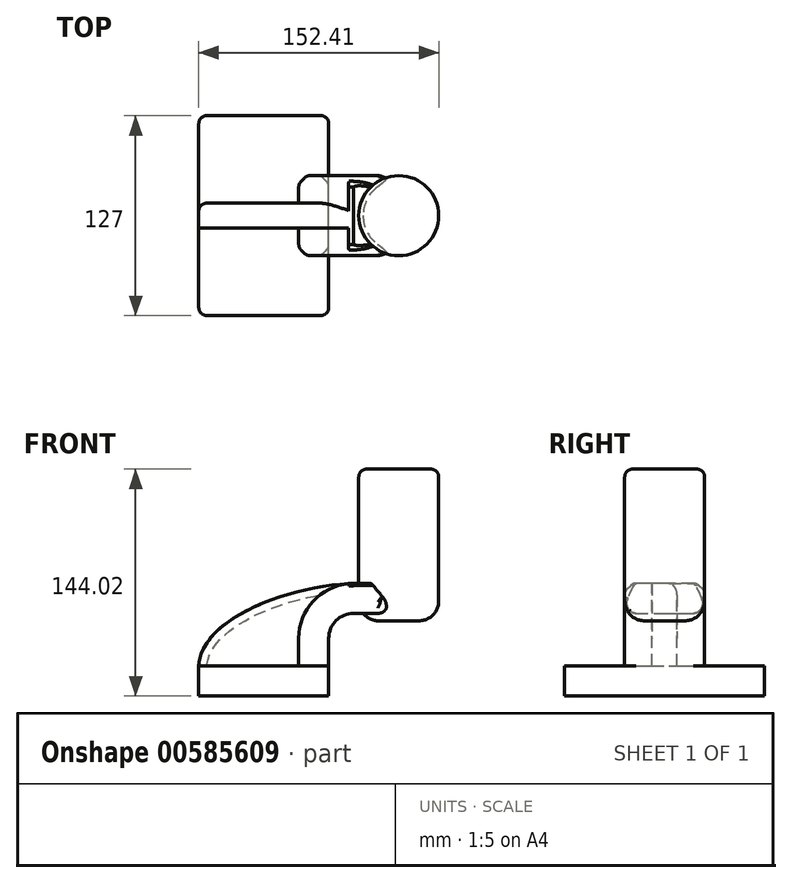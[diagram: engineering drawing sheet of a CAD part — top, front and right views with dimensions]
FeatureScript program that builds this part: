
annotation { "Feature Type Name" : "Feature", "Feature Type Description" : "" }
export const myFeature = defineFeature(function(context is Context, id is Id, definition is map)
    precondition{}
    {
        {
            var Q0;
            Q0=qCreatedBy(makeId("Front.planeOp"),FACE);
            var sketch = newSketch(context, id + "F0", { "sketchPlane" : qUnion([Q0])});
            skLineSegment(sketch, "E0.rect.bottom", {"start": v(-41.28, 9.52) * mm, "end": v(41.28, 9.52) * mm});
            skLineSegment(sketch, "E0.rect.top", {"start": v(-41.28, -9.52) * mm, "end": v(41.28, -9.52) * mm});
            skLineSegment(sketch, "E0.rect.left", {"start": v(-41.28, 9.52) * mm, "end": v(-41.28, -9.52) * mm});
            skLineSegment(sketch, "E0.rect.right", {"start": v(41.28, 9.52) * mm, "end": v(41.28, -9.52) * mm});
            skPoint(sketch, "E0.rect.middle", {"position": v(0, 0) * mm});
            skLineSegment(sketch, "E1", {"start": v(41.28, 9.52) * mm, "end": v(41.28, 27) * mm});
            skArc(sketch, "E2", {"start": v(41.28, 27) * mm, "mid": v(45.92, 38.23) * mm, "end": v(57.15, 42.88) * mm});
            skLineSegment(sketch, "E3", {"start": v(57.15, 42.88) * mm, "end": v(85.72, 42.88) * mm});
            skLineSegment(sketch, "E4.rect.bottom", {"start": v(60.32, 38.1) * mm, "end": v(111.12, 38.1) * mm});
            skLineSegment(sketch, "E4.rect.top", {"start": v(60.32, 66.68) * mm, "end": v(111.12, 66.68) * mm});
            skLineSegment(sketch, "E4.rect.left", {"start": v(60.32, 38.1) * mm, "end": v(60.32, 66.68) * mm});
            skLineSegment(sketch, "E4.rect.right", {"start": v(111.13, 38.1) * mm, "end": v(111.12, 66.68) * mm});
            skPoint(sketch, "E4.rect.middle", {"position": v(85.72, 52.39) * mm});
            skLineSegment(sketch, "E5.0", {"start": v(57.15, 61.93) * mm, "end": v(85.72, 61.93) * mm});
            skArc(sketch, "E5.1", {"start": v(22.23, 27) * mm, "mid": v(32.45, 51.7) * mm, "end": v(57.15, 61.93) * mm});
            skLineSegment(sketch, "E5.2", {"start": v(22.23, 9.52) * mm, "end": v(22.23, 27) * mm});
            skLineSegment(sketch, "E6", {"start": v(85.72, 38.1) * mm, "end": v(85.72, 66.68) * mm});
            skFitSpline(sketch, "E7", {"points": [v(-41.28, 9.53) * mm, v(57.15, 61.93) * mm], "startDerivative": vector(5.2, 92.34) * mm, "endDerivative": vector(120.92, 4.22) * mm});
            skSolve(sketch);
        }
        {
            var Q0;
            Q0=makeQuery(id+"F0.imprint","IMPRINT",FACE,{"disambiguationData":[TD([[makeQuery(id+"F0.imprint","IMPRINT",EDGE,{"derivedFrom":sQuery(id+"F0.wireOp",EDGE,"E0.rect.top")}),1.0]])]});
            extrude(context, id + "F1", {"entities" : qUnion([Q0]), "endBound" : BoundingType.SYMMETRIC, "depth" : 127 * mm});
        }
        {
            var Q0;
            {var subQ9=sQuery(id+"F0.wireOp",EDGE,"E1");Q0=makeQuery(id+"F0.imprint","IMPRINT",FACE,{"disambiguationData":[TD([[makeQuery(id+"F0.imprint","IMPRINT",EDGE,{"derivedFrom":subQ9}),1.0]])]});}
            var Q1;
            {var subQ0=sQuery(id+"F0.wireOp",EDGE,"E6");var subQ1=sQuery(id+"F0.wireOp",EDGE,"E3");var subQ2=makeQuery(id+"F0.imprint","INTERSECT",VERTEX,{"derivedFrom":[subQ1,subQ0]});Q1=makeQuery(id+"F0.imprint","IMPRINT",FACE,{"disambiguationData":[TD([[makeQuery(id+"F0.imprint","IMPRINT",EDGE,{"disambiguationData":[TD([[subQ2,1.0]])],"derivedFrom":subQ1}),1.0]])]});}
            extrude(context, id + "F2", {"entities" : qUnion([Q0, Q1]), "operationType" : NewBodyOperationType.ADD, "endBound" : BoundingType.SYMMETRIC, "depth" : 50.8 * mm});
        }
        {
            var Q0;
            {var subQ3=sQuery(id+"F0.wireOp",EDGE,"E5.2");Q0=makeQuery(id+"F0.imprint","IMPRINT",FACE,{"disambiguationData":[TD([[makeQuery(id+"F0.imprint","IMPRINT",EDGE,{"derivedFrom":subQ3}),1.0]])]});}
            extrude(context, id + "F3", {"entities" : qUnion([Q0]), "operationType" : NewBodyOperationType.ADD, "endBound" : BoundingType.SYMMETRIC, "depth" : 15.88 * mm});
        }
        {
            var Q0;
            {var subQ5=sQuery(id+"F0.wireOp",EDGE,"E4.rect.right");Q0=makeQuery(id+"F0.imprint","IMPRINT",FACE,{"disambiguationData":[TD([[makeQuery(id+"F0.imprint","IMPRINT",EDGE,{"derivedFrom":subQ5}),1.0]])]});}
            var Q1;
            Q1=sQuery(id+"F0.wireOp",EDGE,"E6");
            revolve(context, id + "F4", {"operationType" : NewBodyOperationType.ADD, "entities" : qUnion([Q0]), "axis" : qUnion([Q1]), "revolveType" : RevolveType.FULL});
        }
        {
            var Q0;
            Q0=makeQuery(id+"F1.opExtrude","CAP_EDGE",EDGE,{"disambiguationData":[OSD([sQuery(id+"F0.wireOp",EDGE,"E0.rect.right")])],"isStart":false});
            var Q1;
            Q1=makeQuery(id+"F1.opExtrude","CAP_EDGE",EDGE,{"disambiguationData":[OSD([sQuery(id+"F0.wireOp",EDGE,"E0.rect.left")])],"isStart":false});
            var Q2;
            Q2=makeQuery(id+"F1.opExtrude","CAP_EDGE",EDGE,{"disambiguationData":[OSD([sQuery(id+"F0.wireOp",EDGE,"E0.rect.right")])],"isStart":true});
            var Q3;
            Q3=makeQuery(id+"F1.opExtrude","CAP_EDGE",EDGE,{"disambiguationData":[OSD([sQuery(id+"F0.wireOp",EDGE,"E0.rect.left")])],"isStart":true});
            fillet(context, id + "F5", {"entities" : qUnion([Q0, Q1, Q2, Q3]), "radius" : 5.08 * mm, "tangentPropagation" : true, "allowEdgeOverflow" : false});
        }
        {
            var Q0;
            Q0=makeQuery(id+"F4.opRevolve","SWEPT_FACE",FACE,{"disambiguationData":[OSD([sQuery(id+"F0.wireOp",EDGE,"E4.rect.top")])]});
            extrude(context, id + "F6", {"entities" : qUnion([Q0]), "operationType" : NewBodyOperationType.ADD, "depth" : 67.82 * mm, "offsetDistance" : 25.4 * mm});
        }
        {
            var Q0;
            Q0=makeQuery(id+"F6.opExtrude","CAP_EDGE",EDGE,{"disambiguationData":[OSD([sQuery(id+"F0.wireOp",EDGE,"E4.rect.top"),sQuery(id+"F0.wireOp",EDGE,"E4.rect.right")])],"isStart":false});
            fillet(context, id + "F7", {"entities" : qUnion([Q0]), "radius" : 5.08 * mm, "tangentPropagation" : true, "allowEdgeOverflow" : false});
        }
        {
            var Q0;
            Q0=makeQuery(id+"F2.opExtrude","CAP_EDGE",EDGE,{"disambiguationData":[OSD([sQuery(id+"F0.wireOp",EDGE,"E5.1")])],"isStart":true});
            chamfer(context, id + "F8", {"entities" : qUnion([Q0]), "width" : 5.08 * mm, "tangentPropagation" : true});
        }
        {
            var Q0;
            Q0=makeQuery(id+"F2.opExtrude","CAP_EDGE",EDGE,{"disambiguationData":[OSD([sQuery(id+"F0.wireOp",EDGE,"E5.1")])],"isStart":false});
            chamfer(context, id + "F9", {"entities" : qUnion([Q0]), "width" : 5.08 * mm, "tangentPropagation" : true});
        }
        {
            var Q0;
            Q0=makeQuery(id+"F2.opExtrude","CAP_EDGE",EDGE,{"disambiguationData":[OSD([sQuery(id+"F0.wireOp",EDGE,"E2")])],"isStart":false});
            chamfer(context, id + "F10", {"entities" : qUnion([Q0]), "width" : 5.08 * mm, "tangentPropagation" : true});
        }
        {
            var Q0;
            Q0=makeQuery(id+"F2.opExtrude","CAP_EDGE",EDGE,{"disambiguationData":[OSD([sQuery(id+"F0.wireOp",EDGE,"E2")])],"isStart":true});
            chamfer(context, id + "F11", {"entities" : qUnion([Q0]), "width" : 5.08 * mm, "tangentPropagation" : true});
        }
        {
            var Q0;
            {var subQ0=sQuery(id+"F0.wireOp",EDGE,"E7");var subQ1=sQuery(id+"F0.wireOp",EDGE,"E5.2");var subQ2=sQuery(id+"F0.wireOp",EDGE,"E5.1");var subQ3=sQuery(id+"F0.wireOp",EDGE,"E0.rect.bottom");Q0=makeQuery(id+"F9.opChamfer","BLEND_EDGE",EDGE,{"blendedFrom":[makeQuery(id+"F2.opExtrude","CAP_EDGE",EDGE,{"disambiguationData":[OSD([subQ2])],"isStart":false}),makeQuery(id+"F3.boolean.opBoolean","SPLIT",FACE,{"disambiguationData":[TD([makeQuery(id+"F3.opExtrude","CAP_FACE",FACE,{"disambiguationData":[OSD([subQ3,subQ2,subQ1,subQ0])],"isStart":false})])],"derivedFrom":makeQuery(id+"F2.opExtrude","SWEPT_FACE",FACE,{"disambiguationData":[OSD([subQ2])]})})],"blendedInto":[makeQuery(id+"F3.boolean.opBoolean","SPLIT",FACE,{"disambiguationData":[TD([makeQuery(id+"F3.opExtrude","CAP_FACE",FACE,{"disambiguationData":[OSD([subQ3,subQ2,subQ1,subQ0])],"isStart":false})])],"derivedFrom":makeQuery(id+"F2.opExtrude","SWEPT_FACE",FACE,{"disambiguationData":[OSD([subQ2])]})})]});}
            fillet(context, id + "F12", {"entities" : qUnion([Q0]), "radius" : 5.08 * mm, "tangentPropagation" : true, "allowEdgeOverflow" : false});
        }
        {
            var Q0;
            {var subQ0=sQuery(id+"F0.wireOp",EDGE,"E5.1");Q0=makeQuery(id+"F9.opChamfer","BLEND_EDGE",EDGE,{"blendedFrom":[makeQuery(id+"F2.opExtrude","CAP_EDGE",EDGE,{"disambiguationData":[OSD([subQ0])],"isStart":false}),makeQuery(id+"F2.opExtrude","CAP_FACE",FACE,{"disambiguationData":[OSD([sQuery(id+"F0.wireOp",EDGE,"E0.rect.bottom"),sQuery(id+"F0.wireOp",EDGE,"E1"),sQuery(id+"F0.wireOp",EDGE,"E2"),sQuery(id+"F0.wireOp",EDGE,"E3"),sQuery(id+"F0.wireOp",EDGE,"E5.0"),subQ0,sQuery(id+"F0.wireOp",EDGE,"E5.2"),sQuery(id+"F0.wireOp",EDGE,"E6"),sQuery(id+"F0.wireOp",EDGE,"E7")])],"isStart":false})],"blendedInto":[makeQuery(id+"F2.opExtrude","CAP_FACE",FACE,{"disambiguationData":[OSD([sQuery(id+"F0.wireOp",EDGE,"E0.rect.bottom"),sQuery(id+"F0.wireOp",EDGE,"E1"),sQuery(id+"F0.wireOp",EDGE,"E2"),sQuery(id+"F0.wireOp",EDGE,"E3"),sQuery(id+"F0.wireOp",EDGE,"E5.0"),subQ0,sQuery(id+"F0.wireOp",EDGE,"E5.2"),sQuery(id+"F0.wireOp",EDGE,"E6"),sQuery(id+"F0.wireOp",EDGE,"E7")])],"isStart":false})]});}
            fillet(context, id + "F13", {"entities" : qUnion([Q0]), "radius" : 5.08 * mm, "tangentPropagation" : true, "allowEdgeOverflow" : false});
        }
        {
            var Q0;
            {var subQ0=sQuery(id+"F0.wireOp",EDGE,"E2");Q0=makeQuery(id+"F10.opChamfer","BLEND_EDGE",EDGE,{"blendedFrom":[makeQuery(id+"F2.opExtrude","CAP_EDGE",EDGE,{"disambiguationData":[OSD([subQ0])],"isStart":false}),makeQuery(id+"F2.opExtrude","CAP_FACE",FACE,{"disambiguationData":[OSD([sQuery(id+"F0.wireOp",EDGE,"E0.rect.bottom"),sQuery(id+"F0.wireOp",EDGE,"E1"),subQ0,sQuery(id+"F0.wireOp",EDGE,"E3"),sQuery(id+"F0.wireOp",EDGE,"E5.0"),sQuery(id+"F0.wireOp",EDGE,"E5.1"),sQuery(id+"F0.wireOp",EDGE,"E5.2"),sQuery(id+"F0.wireOp",EDGE,"E6"),sQuery(id+"F0.wireOp",EDGE,"E7")])],"isStart":false})],"blendedInto":[makeQuery(id+"F2.opExtrude","CAP_FACE",FACE,{"disambiguationData":[OSD([sQuery(id+"F0.wireOp",EDGE,"E0.rect.bottom"),sQuery(id+"F0.wireOp",EDGE,"E1"),subQ0,sQuery(id+"F0.wireOp",EDGE,"E3"),sQuery(id+"F0.wireOp",EDGE,"E5.0"),sQuery(id+"F0.wireOp",EDGE,"E5.1"),sQuery(id+"F0.wireOp",EDGE,"E5.2"),sQuery(id+"F0.wireOp",EDGE,"E6"),sQuery(id+"F0.wireOp",EDGE,"E7")])],"isStart":false})]});}
            fillet(context, id + "F14", {"entities" : qUnion([Q0]), "radius" : 5.08 * mm, "tangentPropagation" : true, "allowEdgeOverflow" : false});
        }
        {
            var Q0;
            {var subQ0=sQuery(id+"F0.wireOp",EDGE,"E2");Q0=makeQuery(id+"F10.opChamfer","BLEND_EDGE",EDGE,{"blendedFrom":[makeQuery(id+"F2.opExtrude","CAP_EDGE",EDGE,{"disambiguationData":[OSD([subQ0])],"isStart":false}),makeQuery(id+"F2.opExtrude","SWEPT_FACE",FACE,{"disambiguationData":[OSD([subQ0])]})],"blendedInto":[makeQuery(id+"F2.opExtrude","SWEPT_FACE",FACE,{"disambiguationData":[OSD([subQ0])]})]});}
            var Q1;
            {var subQ0=sQuery(id+"F0.wireOp",EDGE,"E7");var subQ1=sQuery(id+"F0.wireOp",EDGE,"E5.2");var subQ2=sQuery(id+"F0.wireOp",EDGE,"E5.1");var subQ3=sQuery(id+"F0.wireOp",EDGE,"E0.rect.bottom");Q1=makeQuery(id+"F8.opChamfer","BLEND_EDGE",EDGE,{"blendedFrom":[makeQuery(id+"F2.opExtrude","CAP_EDGE",EDGE,{"disambiguationData":[OSD([subQ2])],"isStart":true}),makeQuery(id+"F3.boolean.opBoolean","SPLIT",FACE,{"disambiguationData":[TD([makeQuery(id+"F3.opExtrude","CAP_FACE",FACE,{"disambiguationData":[OSD([subQ3,subQ2,subQ1,subQ0])],"isStart":true})])],"derivedFrom":makeQuery(id+"F2.opExtrude","SWEPT_FACE",FACE,{"disambiguationData":[OSD([subQ2])]})})],"blendedInto":[makeQuery(id+"F3.boolean.opBoolean","SPLIT",FACE,{"disambiguationData":[TD([makeQuery(id+"F3.opExtrude","CAP_FACE",FACE,{"disambiguationData":[OSD([subQ3,subQ2,subQ1,subQ0])],"isStart":true})])],"derivedFrom":makeQuery(id+"F2.opExtrude","SWEPT_FACE",FACE,{"disambiguationData":[OSD([subQ2])]})})]});}
            fillet(context, id + "F15", {"entities" : qUnion([Q0, Q1]), "radius" : 5.08 * mm, "tangentPropagation" : true, "allowEdgeOverflow" : false});
        }
        {
            var Q0;
            {var subQ0=sQuery(id+"F0.wireOp",EDGE,"E5.1");Q0=makeQuery(id+"F8.opChamfer","BLEND_EDGE",EDGE,{"blendedFrom":[makeQuery(id+"F2.opExtrude","CAP_EDGE",EDGE,{"disambiguationData":[OSD([subQ0])],"isStart":true}),makeQuery(id+"F2.opExtrude","CAP_FACE",FACE,{"disambiguationData":[OSD([sQuery(id+"F0.wireOp",EDGE,"E0.rect.bottom"),sQuery(id+"F0.wireOp",EDGE,"E1"),sQuery(id+"F0.wireOp",EDGE,"E2"),sQuery(id+"F0.wireOp",EDGE,"E3"),sQuery(id+"F0.wireOp",EDGE,"E5.0"),subQ0,sQuery(id+"F0.wireOp",EDGE,"E5.2"),sQuery(id+"F0.wireOp",EDGE,"E6"),sQuery(id+"F0.wireOp",EDGE,"E7")])],"isStart":true})],"blendedInto":[makeQuery(id+"F2.opExtrude","CAP_FACE",FACE,{"disambiguationData":[OSD([sQuery(id+"F0.wireOp",EDGE,"E0.rect.bottom"),sQuery(id+"F0.wireOp",EDGE,"E1"),sQuery(id+"F0.wireOp",EDGE,"E2"),sQuery(id+"F0.wireOp",EDGE,"E3"),sQuery(id+"F0.wireOp",EDGE,"E5.0"),subQ0,sQuery(id+"F0.wireOp",EDGE,"E5.2"),sQuery(id+"F0.wireOp",EDGE,"E6"),sQuery(id+"F0.wireOp",EDGE,"E7")])],"isStart":true})]});}
            fillet(context, id + "F16", {"entities" : qUnion([Q0]), "radius" : 5.08 * mm, "tangentPropagation" : true, "allowEdgeOverflow" : false});
        }
        {
            var Q0;
            {var subQ0=sQuery(id+"F0.wireOp",EDGE,"E2");Q0=makeQuery(id+"F11.opChamfer","BLEND_EDGE",EDGE,{"blendedFrom":[makeQuery(id+"F2.opExtrude","CAP_EDGE",EDGE,{"disambiguationData":[OSD([subQ0])],"isStart":true}),makeQuery(id+"F2.opExtrude","SWEPT_FACE",FACE,{"disambiguationData":[OSD([subQ0])]})],"blendedInto":[makeQuery(id+"F2.opExtrude","SWEPT_FACE",FACE,{"disambiguationData":[OSD([subQ0])]})]});}
            fillet(context, id + "F17", {"entities" : qUnion([Q0]), "radius" : 5.08 * mm, "tangentPropagation" : true, "allowEdgeOverflow" : false});
        }
        {
            var Q0;
            {var subQ0=sQuery(id+"F0.wireOp",EDGE,"E2");Q0=makeQuery(id+"F11.opChamfer","BLEND_EDGE",EDGE,{"blendedFrom":[makeQuery(id+"F2.opExtrude","CAP_EDGE",EDGE,{"disambiguationData":[OSD([subQ0])],"isStart":true}),makeQuery(id+"F2.opExtrude","CAP_FACE",FACE,{"disambiguationData":[OSD([sQuery(id+"F0.wireOp",EDGE,"E0.rect.bottom"),sQuery(id+"F0.wireOp",EDGE,"E1"),subQ0,sQuery(id+"F0.wireOp",EDGE,"E3"),sQuery(id+"F0.wireOp",EDGE,"E5.0"),sQuery(id+"F0.wireOp",EDGE,"E5.1"),sQuery(id+"F0.wireOp",EDGE,"E5.2"),sQuery(id+"F0.wireOp",EDGE,"E6"),sQuery(id+"F0.wireOp",EDGE,"E7")])],"isStart":true})],"blendedInto":[makeQuery(id+"F2.opExtrude","CAP_FACE",FACE,{"disambiguationData":[OSD([sQuery(id+"F0.wireOp",EDGE,"E0.rect.bottom"),sQuery(id+"F0.wireOp",EDGE,"E1"),subQ0,sQuery(id+"F0.wireOp",EDGE,"E3"),sQuery(id+"F0.wireOp",EDGE,"E5.0"),sQuery(id+"F0.wireOp",EDGE,"E5.1"),sQuery(id+"F0.wireOp",EDGE,"E5.2"),sQuery(id+"F0.wireOp",EDGE,"E6"),sQuery(id+"F0.wireOp",EDGE,"E7")])],"isStart":true})]});}
            fillet(context, id + "F18", {"entities" : qUnion([Q0]), "radius" : 5.08 * mm, "tangentPropagation" : true, "allowEdgeOverflow" : false});
        }
        {
            var Q0;
            Q0=makeQuery(id+"F3.opExtrude","CAP_EDGE",EDGE,{"disambiguationData":[OSD([sQuery(id+"F0.wireOp",EDGE,"E7")])],"isStart":true});
            var Q1;
            Q1=makeQuery(id+"F3.opExtrude","CAP_EDGE",EDGE,{"disambiguationData":[OSD([sQuery(id+"F0.wireOp",EDGE,"E0.rect.bottom")])],"isStart":false});
            fillet(context, id + "F19", {"entities" : qUnion([Q0, Q1]), "radius" : 5.08 * mm, "tangentPropagation" : true, "allowEdgeOverflow" : false});
        }
        {
            var Q0;
            Q0=makeQuery(id+"F4.opRevolve","SWEPT_EDGE",EDGE,{"disambiguationData":[OSD([sQuery(id+"F0.wireOp",EDGE,"E4.rect.bottom"),sQuery(id+"F0.wireOp",EDGE,"E4.rect.right")])]});
            var Q1;
            Q1=makeQuery(id+"F3.opExtrude","CAP_EDGE",EDGE,{"disambiguationData":[OSD([sQuery(id+"F0.wireOp",EDGE,"E7")])],"isStart":true});
            fillet(context, id + "F20", {"entities" : qUnion([Q0, Q1]), "radius" : 12.7 * mm, "tangentPropagation" : true, "allowEdgeOverflow" : false});
        }
    });
